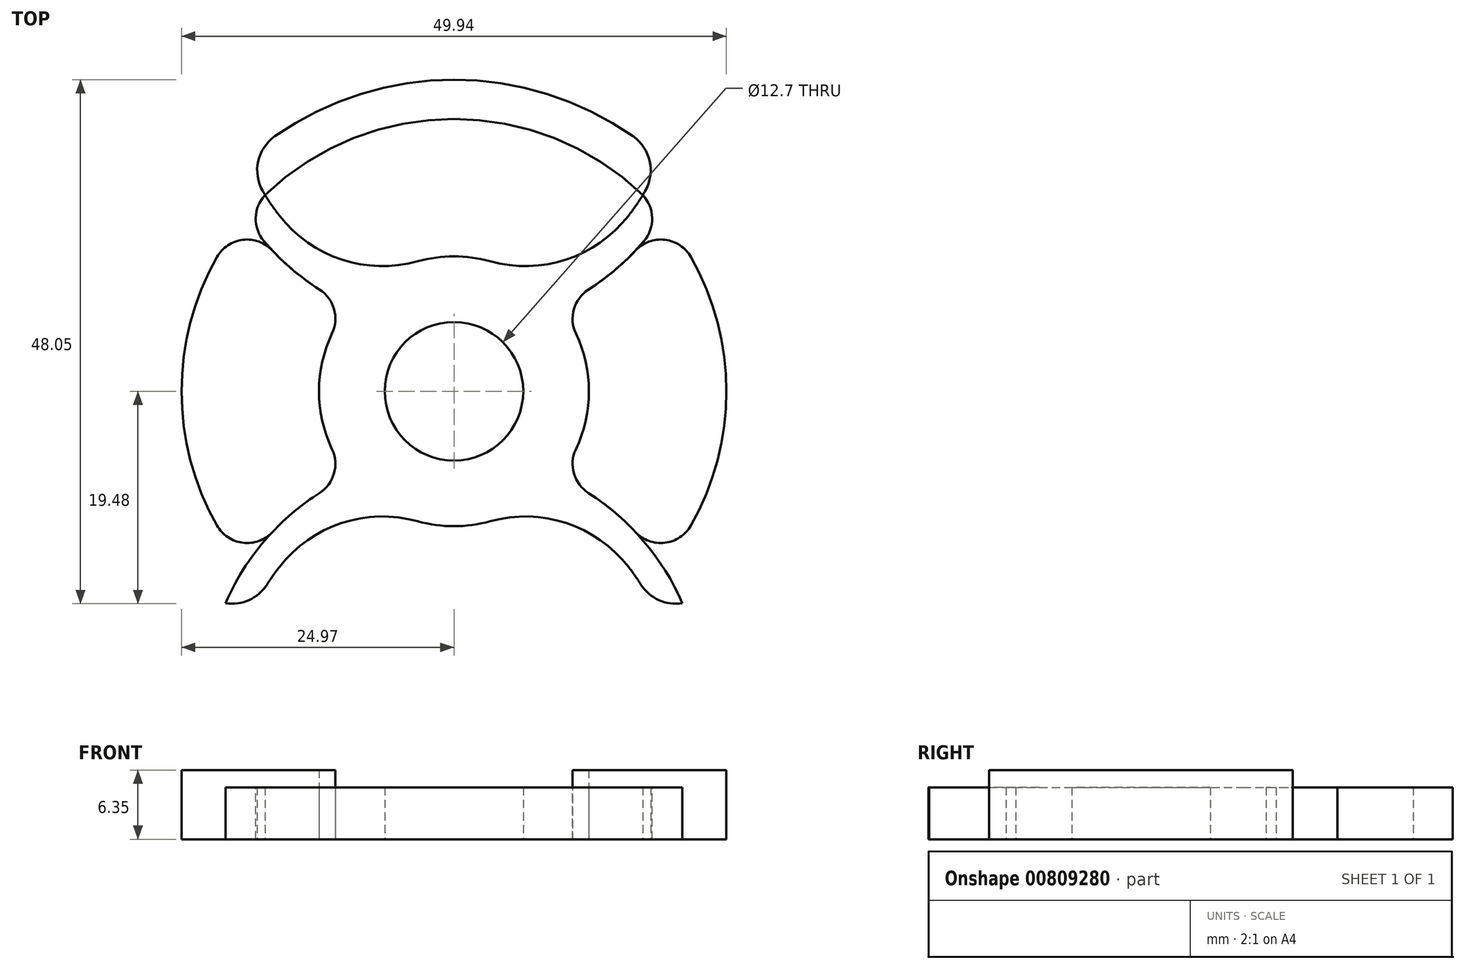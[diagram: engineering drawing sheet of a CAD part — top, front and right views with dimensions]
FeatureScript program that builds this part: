
annotation { "Feature Type Name" : "Feature", "Feature Type Description" : "" }
export const myFeature = defineFeature(function(context is Context, id is Id, definition is map)
    precondition{}
    {
        {
            var Q0;
            Q0=qCreatedBy(makeId("Top.planeOp"),FACE);
            var sketch = newSketch(context, id + "F0", { "sketchPlane" : qUnion([Q0])});
            skCircle(sketch, "E0", {"center": v(0, 0) * mm, "radius": 28.58 * mm});
            skCircle(sketch, "E1", {"center": v(0, 0) * mm, "radius": 12.37 * mm});
            skCircle(sketch, "E2", {"center": v(0, 0) * mm, "radius": 6.35 * mm});
            skLineSegment(sketch, "E3", {"start": v(0, 0) * mm, "end": v(0, 28.58) * mm});
            skLineSegment(sketch, "E4", {"start": v(0, 0) * mm, "end": v(0, -28.58) * mm});
            skArc(sketch, "E5", {"start": v(18.97, -21.37) * mm, "mid": v(0, -8.29) * mm, "end": v(-18.97, -21.37) * mm});
            skArc(sketch, "E6", {"start": v(18.97, 21.37) * mm, "mid": v(0, 8.29) * mm, "end": v(-18.97, 21.37) * mm});
            skCircle(sketch, "E7", {"center": v(0, 0) * mm, "radius": 24.97 * mm});
            skArc(sketch, "E8", {"start": v(-20.95, -19.43) * mm, "mid": v(0, -5.71) * mm, "end": v(20.95, -19.43) * mm});
            skArc(sketch, "E9", {"start": v(20.95, 19.43) * mm, "mid": v(0, 5.71) * mm, "end": v(-20.95, 19.43) * mm});
            skSolve(sketch);
        }
        {
            var Q0;
            {var subQ0=sQuery(id+"F0.wireOp",EDGE,"E5");var subQ1=sQuery(id+"F0.wireOp",EDGE,"E0");var subQ2=makeQuery(id+"F0.imprint","INTERSECT",VERTEX,{"disambiguationData":[OD(1.0)],"derivedFrom":[subQ1,subQ0]});Q0=makeQuery(id+"F0.imprint","IMPRINT",FACE,{"disambiguationData":[TD([[makeQuery(id+"F0.imprint","IMPRINT",EDGE,{"disambiguationData":[TD([[subQ2,1.0]])],"derivedFrom":subQ1}),1.0]])]});}
            var Q1;
            {var subQ0=sQuery(id+"F0.wireOp",EDGE,"E5");var subQ1=sQuery(id+"F0.wireOp",EDGE,"E0");var subQ2=makeQuery(id+"F0.imprint","INTERSECT",VERTEX,{"disambiguationData":[OD(0.0)],"derivedFrom":[subQ1,subQ0]});Q1=makeQuery(id+"F0.imprint","IMPRINT",FACE,{"disambiguationData":[TD([[makeQuery(id+"F0.imprint","IMPRINT",EDGE,{"disambiguationData":[TD([[subQ2,-1.0]])],"derivedFrom":subQ1}),1.0]])]});}
            var Q2;
            {var subQ0=sQuery(id+"F0.wireOp",EDGE,"E6");var subQ1=sQuery(id+"F0.wireOp",EDGE,"E1");var subQ2=makeQuery(id+"F0.imprint","INTERSECT",VERTEX,{"disambiguationData":[OD(0.0)],"derivedFrom":[subQ1,subQ0]});Q2=makeQuery(id+"F0.imprint","IMPRINT",FACE,{"disambiguationData":[TD([[makeQuery(id+"F0.imprint","IMPRINT",EDGE,{"disambiguationData":[TD([[subQ2,1.0]])],"derivedFrom":subQ1}),1.0]])]});}
            var Q3;
            {var subQ0=sQuery(id+"F0.wireOp",EDGE,"E6");var subQ1=sQuery(id+"F0.wireOp",EDGE,"E1");var subQ2=makeQuery(id+"F0.imprint","INTERSECT",VERTEX,{"disambiguationData":[OD(0.0)],"derivedFrom":[subQ1,subQ0]});Q3=makeQuery(id+"F0.imprint","IMPRINT",FACE,{"disambiguationData":[TD([[makeQuery(id+"F0.imprint","IMPRINT",EDGE,{"disambiguationData":[TD([[subQ2,-1.0]])],"derivedFrom":subQ1}),1.0]])]});}
            var Q4;
            {var subQ0=sQuery(id+"F0.wireOp",EDGE,"E3");var subQ1=sQuery(id+"F0.wireOp",EDGE,"E1");var subQ2=makeQuery(id+"F0.imprint","INTERSECT",VERTEX,{"derivedFrom":[subQ1,subQ0]});Q4=makeQuery(id+"F0.imprint","IMPRINT",FACE,{"disambiguationData":[TD([[makeQuery(id+"F0.imprint","IMPRINT",EDGE,{"disambiguationData":[TD([[subQ2,-1.0]])],"derivedFrom":subQ1}),1.0]])]});}
            var Q5;
            {var subQ0=sQuery(id+"F0.wireOp",EDGE,"E6");var subQ1=sQuery(id+"F0.wireOp",EDGE,"E1");var subQ2=makeQuery(id+"F0.imprint","INTERSECT",VERTEX,{"disambiguationData":[OD(1.0)],"derivedFrom":[subQ1,subQ0]});Q5=makeQuery(id+"F0.imprint","IMPRINT",FACE,{"disambiguationData":[TD([[makeQuery(id+"F0.imprint","IMPRINT",EDGE,{"disambiguationData":[TD([[subQ2,-1.0]])],"derivedFrom":subQ1}),1.0]])]});}
            var Q6;
            {var subQ0=sQuery(id+"F0.wireOp",EDGE,"E5");var subQ1=sQuery(id+"F0.wireOp",EDGE,"E1");var subQ2=makeQuery(id+"F0.imprint","INTERSECT",VERTEX,{"disambiguationData":[OD(0.0)],"derivedFrom":[subQ1,subQ0]});Q6=makeQuery(id+"F0.imprint","IMPRINT",FACE,{"disambiguationData":[TD([[makeQuery(id+"F0.imprint","IMPRINT",EDGE,{"disambiguationData":[TD([[subQ2,-1.0]])],"derivedFrom":subQ1}),1.0]])]});}
            var Q7;
            {var subQ0=sQuery(id+"F0.wireOp",EDGE,"E4");var subQ1=sQuery(id+"F0.wireOp",EDGE,"E1");var subQ2=makeQuery(id+"F0.imprint","INTERSECT",VERTEX,{"derivedFrom":[subQ1,subQ0]});Q7=makeQuery(id+"F0.imprint","IMPRINT",FACE,{"disambiguationData":[TD([[makeQuery(id+"F0.imprint","IMPRINT",EDGE,{"disambiguationData":[TD([[subQ2,-1.0]])],"derivedFrom":subQ1}),1.0]])]});}
            var Q8;
            {var subQ0=sQuery(id+"F0.wireOp",EDGE,"E6");var subQ1=sQuery(id+"F0.wireOp",EDGE,"E1");var subQ2=makeQuery(id+"F0.imprint","INTERSECT",VERTEX,{"disambiguationData":[OD(1.0)],"derivedFrom":[subQ1,subQ0]});Q8=makeQuery(id+"F0.imprint","IMPRINT",FACE,{"disambiguationData":[TD([[makeQuery(id+"F0.imprint","IMPRINT",EDGE,{"disambiguationData":[TD([[subQ2,-1.0]])],"derivedFrom":subQ1}),-1.0]])]});}
            var Q9;
            {var subQ0=sQuery(id+"F0.wireOp",EDGE,"E6");var subQ1=sQuery(id+"F0.wireOp",EDGE,"E0");var subQ2=makeQuery(id+"F0.imprint","INTERSECT",VERTEX,{"disambiguationData":[OD(1.0)],"derivedFrom":[subQ1,subQ0]});Q9=makeQuery(id+"F0.imprint","IMPRINT",FACE,{"disambiguationData":[TD([[makeQuery(id+"F0.imprint","IMPRINT",EDGE,{"disambiguationData":[TD([[subQ2,-1.0]])],"derivedFrom":subQ1}),1.0]])]});}
            var Q10;
            {var subQ0=sQuery(id+"F0.wireOp",EDGE,"E8");var subQ1=sQuery(id+"F0.wireOp",EDGE,"E0");var subQ2=makeQuery(id+"F0.imprint","INTERSECT",VERTEX,{"disambiguationData":[OD(0.0)],"derivedFrom":[subQ1,subQ0]});Q10=makeQuery(id+"F0.imprint","IMPRINT",FACE,{"disambiguationData":[TD([[makeQuery(id+"F0.imprint","IMPRINT",EDGE,{"disambiguationData":[TD([[subQ2,1.0]])],"derivedFrom":subQ1}),1.0]])]});}
            var Q11;
            {var subQ0=sQuery(id+"F0.wireOp",EDGE,"E8");var subQ1=sQuery(id+"F0.wireOp",EDGE,"E1");var subQ2=makeQuery(id+"F0.imprint","INTERSECT",VERTEX,{"disambiguationData":[OD(0.0)],"derivedFrom":[subQ1,subQ0]});Q11=makeQuery(id+"F0.imprint","IMPRINT",FACE,{"disambiguationData":[TD([[makeQuery(id+"F0.imprint","IMPRINT",EDGE,{"disambiguationData":[TD([[subQ2,-1.0]])],"derivedFrom":subQ1}),-1.0]])]});}
            var Q12;
            {var subQ1=sQuery(id+"F0.wireOp",EDGE,"E1");var subQ7=sQuery(id+"F0.wireOp",EDGE,"E8");var subQ9=makeQuery(id+"F0.imprint","INTERSECT",VERTEX,{"disambiguationData":[OD(0.0)],"derivedFrom":[subQ1,subQ7]});Q12=makeQuery(id+"F0.imprint","IMPRINT",FACE,{"disambiguationData":[TD([[makeQuery(id+"F0.imprint","IMPRINT",EDGE,{"disambiguationData":[TD([[subQ9,-1.0]])],"derivedFrom":subQ1}),1.0]])]});}
            var Q13;
            {var subQ0=sQuery(id+"F0.wireOp",EDGE,"E5");var subQ1=sQuery(id+"F0.wireOp",EDGE,"E1");var subQ2=makeQuery(id+"F0.imprint","INTERSECT",VERTEX,{"disambiguationData":[OD(1.0)],"derivedFrom":[subQ1,subQ0]});Q13=makeQuery(id+"F0.imprint","IMPRINT",FACE,{"disambiguationData":[TD([[makeQuery(id+"F0.imprint","IMPRINT",EDGE,{"disambiguationData":[TD([[subQ2,-1.0]])],"derivedFrom":subQ1}),1.0]])]});}
            var Q14;
            {var subQ0=sQuery(id+"F0.wireOp",EDGE,"E5");var subQ1=sQuery(id+"F0.wireOp",EDGE,"E1");var subQ2=makeQuery(id+"F0.imprint","INTERSECT",VERTEX,{"disambiguationData":[OD(1.0)],"derivedFrom":[subQ1,subQ0]});Q14=makeQuery(id+"F0.imprint","IMPRINT",FACE,{"disambiguationData":[TD([[makeQuery(id+"F0.imprint","IMPRINT",EDGE,{"disambiguationData":[TD([[subQ2,-1.0]])],"derivedFrom":subQ1}),-1.0]])]});}
            var Q15;
            {var subQ0=sQuery(id+"F0.wireOp",EDGE,"E8");var subQ1=sQuery(id+"F0.wireOp",EDGE,"E0");var subQ2=makeQuery(id+"F0.imprint","INTERSECT",VERTEX,{"disambiguationData":[OD(1.0)],"derivedFrom":[subQ1,subQ0]});Q15=makeQuery(id+"F0.imprint","IMPRINT",FACE,{"disambiguationData":[TD([[makeQuery(id+"F0.imprint","IMPRINT",EDGE,{"disambiguationData":[TD([[subQ2,-1.0]])],"derivedFrom":subQ1}),1.0]])]});}
            var Q16;
            {var subQ0=sQuery(id+"F0.wireOp",EDGE,"E6");var subQ1=sQuery(id+"F0.wireOp",EDGE,"E1");var subQ2=makeQuery(id+"F0.imprint","INTERSECT",VERTEX,{"disambiguationData":[OD(0.0)],"derivedFrom":[subQ1,subQ0]});Q16=makeQuery(id+"F0.imprint","IMPRINT",FACE,{"disambiguationData":[TD([[makeQuery(id+"F0.imprint","IMPRINT",EDGE,{"disambiguationData":[TD([[subQ2,1.0]])],"derivedFrom":subQ1}),-1.0]])]});}
            var Q17;
            {var subQ0=sQuery(id+"F0.wireOp",EDGE,"E6");var subQ1=sQuery(id+"F0.wireOp",EDGE,"E0");var subQ2=makeQuery(id+"F0.imprint","INTERSECT",VERTEX,{"disambiguationData":[OD(0.0)],"derivedFrom":[subQ1,subQ0]});Q17=makeQuery(id+"F0.imprint","IMPRINT",FACE,{"disambiguationData":[TD([[makeQuery(id+"F0.imprint","IMPRINT",EDGE,{"disambiguationData":[TD([[subQ2,1.0]])],"derivedFrom":subQ1}),1.0]])]});}
            var Q18;
            {var subQ0=sQuery(id+"F0.wireOp",EDGE,"E9");var subQ1=sQuery(id+"F0.wireOp",EDGE,"E1");var subQ2=makeQuery(id+"F0.imprint","INTERSECT",VERTEX,{"disambiguationData":[OD(0.0)],"derivedFrom":[subQ1,subQ0]});Q18=makeQuery(id+"F0.imprint","IMPRINT",FACE,{"disambiguationData":[TD([[makeQuery(id+"F0.imprint","IMPRINT",EDGE,{"disambiguationData":[TD([[subQ2,1.0]])],"derivedFrom":subQ1}),1.0]])]});}
            var Q19;
            {var subQ0=sQuery(id+"F0.wireOp",EDGE,"E9");var subQ1=sQuery(id+"F0.wireOp",EDGE,"E1");var subQ2=makeQuery(id+"F0.imprint","INTERSECT",VERTEX,{"disambiguationData":[OD(1.0)],"derivedFrom":[subQ1,subQ0]});Q19=makeQuery(id+"F0.imprint","IMPRINT",FACE,{"disambiguationData":[TD([[makeQuery(id+"F0.imprint","IMPRINT",EDGE,{"disambiguationData":[TD([[subQ2,-1.0]])],"derivedFrom":subQ1}),1.0]])]});}
            extrude(context, id + "F1", {"entities" : qUnion([Q0, Q1, Q2, Q3, Q4, Q5, Q6, Q7, Q8, Q9, Q10, Q11, Q12, Q13, Q14, Q15, Q16, Q17, Q18, Q19]), "depth" : 4.76 * mm, "offsetDistance" : 25.4 * mm});
        }
        {
            var Q0;
            {var subQ0=sQuery(id+"F0.wireOp",EDGE,"E5");var subQ1=sQuery(id+"F0.wireOp",EDGE,"E0");Q0=makeQuery(id+"F1.opExtrude","SWEPT_EDGE",EDGE,{"disambiguationData":[OSD([subQ1,subQ0]),TDD([makeQuery(id+"F0.imprint","INTERSECT",VERTEX,{"disambiguationData":[OD(0.0)],"derivedFrom":[subQ1,subQ0]})])]});}
            var Q1;
            {var subQ0=sQuery(id+"F0.wireOp",EDGE,"E5");var subQ1=sQuery(id+"F0.wireOp",EDGE,"E0");Q1=makeQuery(id+"F1.opExtrude","SWEPT_EDGE",EDGE,{"disambiguationData":[OSD([subQ1,subQ0]),TDD([makeQuery(id+"F0.imprint","INTERSECT",VERTEX,{"disambiguationData":[OD(1.0)],"derivedFrom":[subQ1,subQ0]})])]});}
            var Q2;
            {var subQ0=sQuery(id+"F0.wireOp",EDGE,"E6");var subQ1=sQuery(id+"F0.wireOp",EDGE,"E0");Q2=makeQuery(id+"F1.opExtrude","SWEPT_EDGE",EDGE,{"disambiguationData":[OSD([subQ1,subQ0]),TDD([makeQuery(id+"F0.imprint","INTERSECT",VERTEX,{"disambiguationData":[OD(0.0)],"derivedFrom":[subQ1,subQ0]})])]});}
            var Q3;
            {var subQ0=sQuery(id+"F0.wireOp",EDGE,"E6");var subQ1=sQuery(id+"F0.wireOp",EDGE,"E0");Q3=makeQuery(id+"F1.opExtrude","SWEPT_EDGE",EDGE,{"disambiguationData":[OSD([subQ1,subQ0]),TDD([makeQuery(id+"F0.imprint","INTERSECT",VERTEX,{"disambiguationData":[OD(1.0)],"derivedFrom":[subQ1,subQ0]})])]});}
            fillet(context, id + "F2", {"entities" : qUnion([Q0, Q1, Q2, Q3]), "radius" : 3.8 * mm, "tangentPropagation" : true, "allowEdgeOverflow" : false});
        }
        {
            var Q0;
            {var subQ0=sQuery(id+"F0.wireOp",EDGE,"E5");var subQ1=sQuery(id+"F0.wireOp",EDGE,"E1");Q0=makeQuery(id+"F1.opExtrude","SWEPT_EDGE",EDGE,{"disambiguationData":[OSD([subQ1,subQ0]),TDD([makeQuery(id+"F0.imprint","INTERSECT",VERTEX,{"disambiguationData":[OD(0.0)],"derivedFrom":[subQ1,subQ0]})])]});}
            var Q1;
            {var subQ0=sQuery(id+"F0.wireOp",EDGE,"E6");var subQ1=sQuery(id+"F0.wireOp",EDGE,"E1");Q1=makeQuery(id+"F1.opExtrude","SWEPT_EDGE",EDGE,{"disambiguationData":[OSD([subQ1,subQ0]),TDD([makeQuery(id+"F0.imprint","INTERSECT",VERTEX,{"disambiguationData":[OD(0.0)],"derivedFrom":[subQ1,subQ0]})])]});}
            var Q2;
            {var subQ0=sQuery(id+"F0.wireOp",EDGE,"E6");var subQ1=sQuery(id+"F0.wireOp",EDGE,"E1");Q2=makeQuery(id+"F1.opExtrude","SWEPT_EDGE",EDGE,{"disambiguationData":[OSD([subQ1,subQ0]),TDD([makeQuery(id+"F0.imprint","INTERSECT",VERTEX,{"disambiguationData":[OD(1.0)],"derivedFrom":[subQ1,subQ0]})])]});}
            var Q3;
            {var subQ0=sQuery(id+"F0.wireOp",EDGE,"E5");var subQ1=sQuery(id+"F0.wireOp",EDGE,"E1");Q3=makeQuery(id+"F1.opExtrude","SWEPT_EDGE",EDGE,{"disambiguationData":[OSD([subQ1,subQ0]),TDD([makeQuery(id+"F0.imprint","INTERSECT",VERTEX,{"disambiguationData":[OD(1.0)],"derivedFrom":[subQ1,subQ0]})])]});}
            fillet(context, id + "F3", {"entities" : qUnion([Q0, Q1, Q2, Q3]), "radius" : 12 * mm, "tangentPropagation" : true, "allowEdgeOverflow" : false});
        }
        {
            var Q0;
            {var subQ0=sQuery(id+"F0.wireOp",EDGE,"E9");var subQ1=sQuery(id+"F0.wireOp",EDGE,"E7");Q0=makeQuery(id+"F1.opExtrude","SWEPT_EDGE",EDGE,{"disambiguationData":[OSD([subQ1,subQ0]),TDD([makeQuery(id+"F0.imprint","INTERSECT",VERTEX,{"disambiguationData":[OD(1.0)],"derivedFrom":[subQ1,subQ0]})])]});}
            var Q1;
            {var subQ0=sQuery(id+"F0.wireOp",EDGE,"E9");var subQ1=sQuery(id+"F0.wireOp",EDGE,"E7");Q1=makeQuery(id+"F1.opExtrude","SWEPT_EDGE",EDGE,{"disambiguationData":[OSD([subQ1,subQ0]),TDD([makeQuery(id+"F0.imprint","INTERSECT",VERTEX,{"disambiguationData":[OD(0.0)],"derivedFrom":[subQ1,subQ0]})])]});}
            var Q2;
            {var subQ0=sQuery(id+"F0.wireOp",EDGE,"E8");var subQ1=sQuery(id+"F0.wireOp",EDGE,"E7");Q2=makeQuery(id+"F1.opExtrude","SWEPT_EDGE",EDGE,{"disambiguationData":[OSD([subQ1,subQ0]),TDD([makeQuery(id+"F0.imprint","INTERSECT",VERTEX,{"disambiguationData":[OD(0.0)],"derivedFrom":[subQ1,subQ0]})])]});}
            var Q3;
            {var subQ0=sQuery(id+"F0.wireOp",EDGE,"E8");var subQ1=sQuery(id+"F0.wireOp",EDGE,"E7");Q3=makeQuery(id+"F1.opExtrude","SWEPT_EDGE",EDGE,{"disambiguationData":[OSD([subQ1,subQ0]),TDD([makeQuery(id+"F0.imprint","INTERSECT",VERTEX,{"disambiguationData":[OD(1.0)],"derivedFrom":[subQ1,subQ0]})])]});}
            var Q4;
            {var subQ0=sQuery(id+"F0.wireOp",EDGE,"E9");var subQ1=sQuery(id+"F0.wireOp",EDGE,"E1");Q4=makeQuery(id+"F1.opExtrude","SWEPT_EDGE",EDGE,{"disambiguationData":[OSD([subQ1,subQ0]),TDD([makeQuery(id+"F0.imprint","INTERSECT",VERTEX,{"disambiguationData":[OD(0.0)],"derivedFrom":[subQ1,subQ0]})])]});}
            var Q5;
            {var subQ0=sQuery(id+"F0.wireOp",EDGE,"E8");var subQ1=sQuery(id+"F0.wireOp",EDGE,"E1");Q5=makeQuery(id+"F1.opExtrude","SWEPT_EDGE",EDGE,{"disambiguationData":[OSD([subQ1,subQ0]),TDD([makeQuery(id+"F0.imprint","INTERSECT",VERTEX,{"disambiguationData":[OD(1.0)],"derivedFrom":[subQ1,subQ0]})])]});}
            var Q6;
            {var subQ0=sQuery(id+"F0.wireOp",EDGE,"E9");var subQ1=sQuery(id+"F0.wireOp",EDGE,"E1");Q6=makeQuery(id+"F1.opExtrude","SWEPT_EDGE",EDGE,{"disambiguationData":[OSD([subQ1,subQ0]),TDD([makeQuery(id+"F0.imprint","INTERSECT",VERTEX,{"disambiguationData":[OD(1.0)],"derivedFrom":[subQ1,subQ0]})])]});}
            var Q7;
            {var subQ0=sQuery(id+"F0.wireOp",EDGE,"E8");var subQ1=sQuery(id+"F0.wireOp",EDGE,"E1");Q7=makeQuery(id+"F1.opExtrude","SWEPT_EDGE",EDGE,{"disambiguationData":[OSD([subQ1,subQ0]),TDD([makeQuery(id+"F0.imprint","INTERSECT",VERTEX,{"disambiguationData":[OD(0.0)],"derivedFrom":[subQ1,subQ0]})])]});}
            fillet(context, id + "F4", {"entities" : qUnion([Q0, Q1, Q2, Q3, Q4, Q5, Q6, Q7]), "radius" : 3.17 * mm, "tangentPropagation" : true, "allowEdgeOverflow" : false});
        }
        {
            var Q0;
            {var subQ0=sQuery(id+"F0.wireOp",EDGE,"E9");var subQ1=sQuery(id+"F0.wireOp",EDGE,"E1");var subQ2=makeQuery(id+"F0.imprint","INTERSECT",VERTEX,{"disambiguationData":[OD(1.0)],"derivedFrom":[subQ1,subQ0]});Q0=makeQuery(id+"F0.imprint","IMPRINT",FACE,{"disambiguationData":[TD([[makeQuery(id+"F0.imprint","IMPRINT",EDGE,{"disambiguationData":[TD([[subQ2,-1.0]])],"derivedFrom":subQ1}),-1.0]])]});}
            var Q1;
            {var subQ0=sQuery(id+"F0.wireOp",EDGE,"E9");var subQ1=sQuery(id+"F0.wireOp",EDGE,"E1");var subQ2=makeQuery(id+"F0.imprint","INTERSECT",VERTEX,{"disambiguationData":[OD(0.0)],"derivedFrom":[subQ1,subQ0]});Q1=makeQuery(id+"F0.imprint","IMPRINT",FACE,{"disambiguationData":[TD([[makeQuery(id+"F0.imprint","IMPRINT",EDGE,{"disambiguationData":[TD([[subQ2,1.0]])],"derivedFrom":subQ1}),-1.0]])]});}
            extrude(context, id + "F5", {"entities" : qUnion([Q0, Q1]), "depth" : 6.35 * mm, "offsetDistance" : 25.4 * mm});
        }
        {
            var Q0;
            {var subQ0=sQuery(id+"F0.wireOp",EDGE,"E9");var subQ1=sQuery(id+"F0.wireOp",EDGE,"E7");Q0=makeQuery(id+"F5.opExtrude","SWEPT_EDGE",EDGE,{"disambiguationData":[OSD([subQ1,subQ0]),TDD([makeQuery(id+"F0.imprint","INTERSECT",VERTEX,{"disambiguationData":[OD(1.0)],"derivedFrom":[subQ1,subQ0]})])]});}
            var Q1;
            {var subQ0=sQuery(id+"F0.wireOp",EDGE,"E9");var subQ1=sQuery(id+"F0.wireOp",EDGE,"E1");Q1=makeQuery(id+"F5.opExtrude","SWEPT_EDGE",EDGE,{"disambiguationData":[OSD([subQ1,subQ0]),TDD([makeQuery(id+"F0.imprint","INTERSECT",VERTEX,{"disambiguationData":[OD(1.0)],"derivedFrom":[subQ1,subQ0]})])]});}
            var Q2;
            {var subQ0=sQuery(id+"F0.wireOp",EDGE,"E8");var subQ1=sQuery(id+"F0.wireOp",EDGE,"E1");Q2=makeQuery(id+"F5.opExtrude","SWEPT_EDGE",EDGE,{"disambiguationData":[OSD([subQ1,subQ0]),TDD([makeQuery(id+"F0.imprint","INTERSECT",VERTEX,{"disambiguationData":[OD(0.0)],"derivedFrom":[subQ1,subQ0]})])]});}
            var Q3;
            {var subQ0=sQuery(id+"F0.wireOp",EDGE,"E8");var subQ1=sQuery(id+"F0.wireOp",EDGE,"E1");Q3=makeQuery(id+"F5.opExtrude","SWEPT_EDGE",EDGE,{"disambiguationData":[OSD([subQ1,subQ0]),TDD([makeQuery(id+"F0.imprint","INTERSECT",VERTEX,{"disambiguationData":[OD(1.0)],"derivedFrom":[subQ1,subQ0]})])]});}
            var Q4;
            {var subQ0=sQuery(id+"F0.wireOp",EDGE,"E9");var subQ1=sQuery(id+"F0.wireOp",EDGE,"E1");Q4=makeQuery(id+"F5.opExtrude","SWEPT_EDGE",EDGE,{"disambiguationData":[OSD([subQ1,subQ0]),TDD([makeQuery(id+"F0.imprint","INTERSECT",VERTEX,{"disambiguationData":[OD(0.0)],"derivedFrom":[subQ1,subQ0]})])]});}
            var Q5;
            {var subQ0=sQuery(id+"F0.wireOp",EDGE,"E9");var subQ1=sQuery(id+"F0.wireOp",EDGE,"E7");Q5=makeQuery(id+"F5.opExtrude","SWEPT_EDGE",EDGE,{"disambiguationData":[OSD([subQ1,subQ0]),TDD([makeQuery(id+"F0.imprint","INTERSECT",VERTEX,{"disambiguationData":[OD(0.0)],"derivedFrom":[subQ1,subQ0]})])]});}
            var Q6;
            {var subQ0=sQuery(id+"F0.wireOp",EDGE,"E8");var subQ1=sQuery(id+"F0.wireOp",EDGE,"E7");Q6=makeQuery(id+"F5.opExtrude","SWEPT_EDGE",EDGE,{"disambiguationData":[OSD([subQ1,subQ0]),TDD([makeQuery(id+"F0.imprint","INTERSECT",VERTEX,{"disambiguationData":[OD(0.0)],"derivedFrom":[subQ1,subQ0]})])]});}
            var Q7;
            {var subQ0=sQuery(id+"F0.wireOp",EDGE,"E8");var subQ1=sQuery(id+"F0.wireOp",EDGE,"E7");Q7=makeQuery(id+"F5.opExtrude","SWEPT_EDGE",EDGE,{"disambiguationData":[OSD([subQ1,subQ0]),TDD([makeQuery(id+"F0.imprint","INTERSECT",VERTEX,{"disambiguationData":[OD(1.0)],"derivedFrom":[subQ1,subQ0]})])]});}
            fillet(context, id + "F6", {"entities" : qUnion([Q0, Q1, Q2, Q3, Q4, Q5, Q6, Q7]), "radius" : 3.17 * mm, "tangentPropagation" : true, "allowEdgeOverflow" : false});
        }
    });
